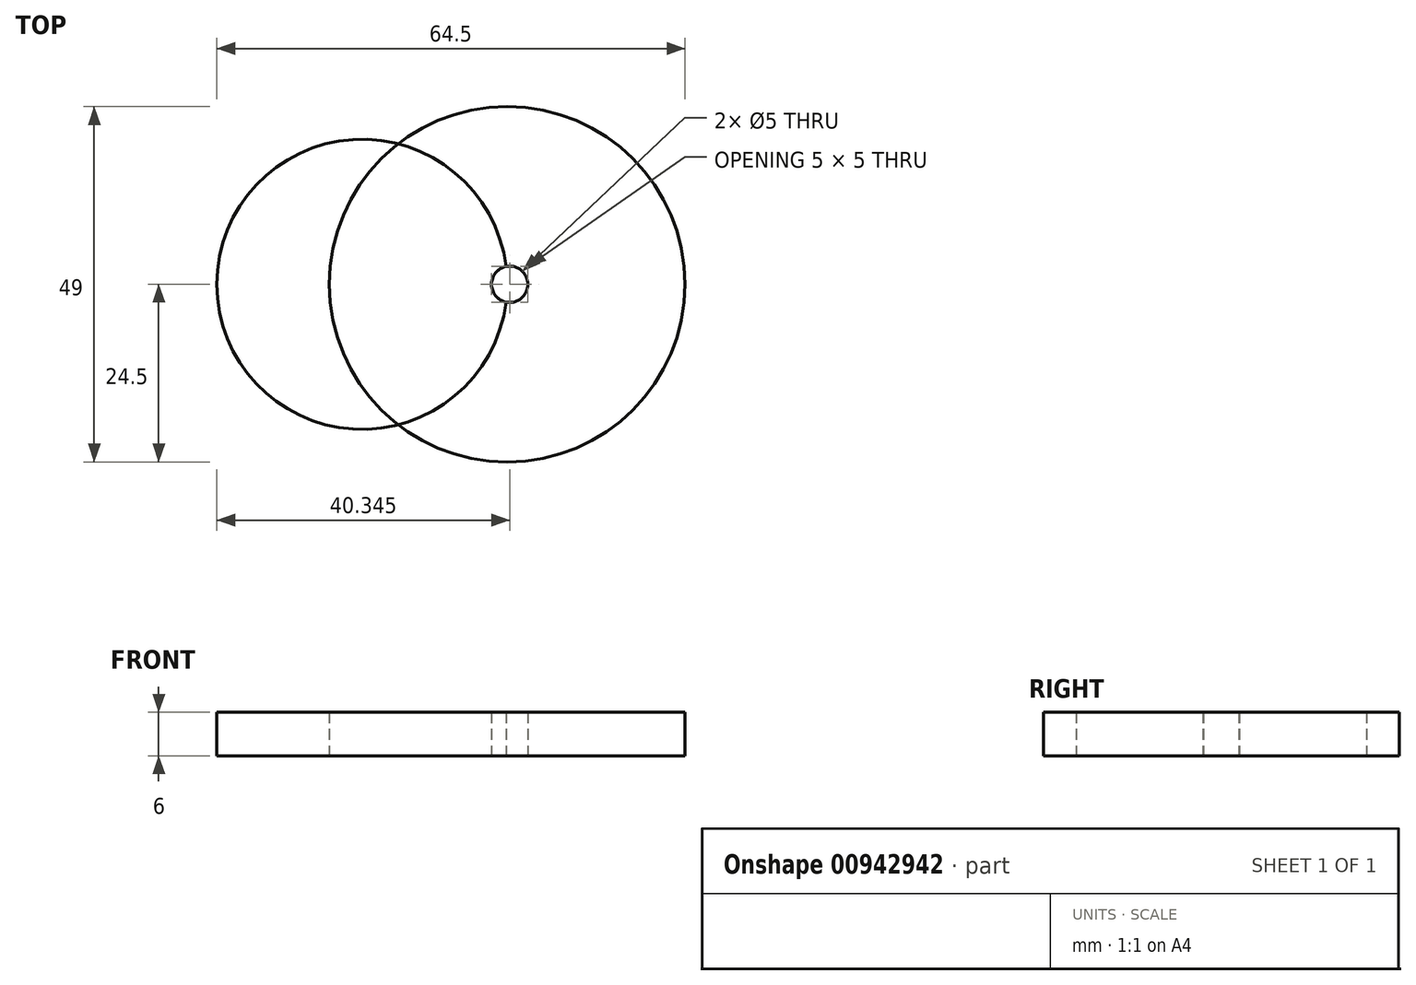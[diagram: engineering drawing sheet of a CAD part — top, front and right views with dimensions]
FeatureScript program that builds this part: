
annotation { "Feature Type Name" : "Feature", "Feature Type Description" : "" }
export const myFeature = defineFeature(function(context is Context, id is Id, definition is map)
    precondition{}
    {
        {
            var Q0;
            Q0=qCreatedBy(makeId("Top.planeOp"),FACE);
            var sketch = newSketch(context, id + "F0", { "sketchPlane" : qUnion([Q0])});
            skCircle(sketch, "E0", {"center": v(0, 0) * mm, "radius": 20 * mm});
            skSolve(sketch);
        }
        {
            var Q0;
            Q0 = qSketchRegion(id + "F0", true);
            extrude(context, id + "F1", {"entities" : qUnion([Q0]), "depth" : 6 * mm, "offsetDistance" : 25 * mm});
        }
        {
            var Q0;
            Q0=qCreatedBy(makeId("Front.planeOp"),FACE);
            var sketch = newSketch(context, id + "F2", { "sketchPlane" : qUnion([Q0])});
            skArc(sketch, "E1", {"start": v(0, 12) * mm, "mid": v(-6, 6) * mm, "end": v(0, 0) * mm});
            skSolve(sketch);
        }
        {
            var Q0;
            Q0=sQuery(id+"F2.wireOp",EDGE,"E1");
            var Q1;
            Q1=makeQuery(id+"F1.opExtrude","CAP_EDGE",EDGE,{"disambiguationData":[OSD([sQuery(id+"F0.wireOp",EDGE,"E0")])],"isStart":false});
            revolve(context, id + "F3", {"bodyType" : ToolBodyType.SURFACE, "surfaceOperationType" : NewSurfaceOperationType.NEW, "surfaceEntities" : qUnion([Q0]), "axis" : qUnion([Q1]), "revolveType" : RevolveType.FULL});
        }
        {
            var Q0;
            Q0=qCreatedBy(makeId("Top.planeOp"),FACE);
            var sketch = newSketch(context, id + "F4", { "sketchPlane" : qUnion([Q0])});
            skCircle(sketch, "E2", {"center": v(20, 0) * mm, "radius": 24.5 * mm});
            skSolve(sketch);
        }
        {
            var Q0;
            Q0 = qSketchRegion(id + "F4", true);
            extrude(context, id + "F5", {"entities" : qUnion([Q0]), "depth" : 6 * mm, "offsetDistance" : 25 * mm});
        }
        {
            var Q0;
            Q0=makeQuery(id+"F3.opRevolve","SWEPT_BODY",BODY,{"disambiguationData":[OSD([sQuery(id+"F2.wireOp",EDGE,"E1")])]});
            var Q1;
            Q1=makeQuery(id+"F5.opExtrude","CAP_EDGE",EDGE,{"disambiguationData":[OSD([sQuery(id+"F4.wireOp",EDGE,"E2")])],"isStart":false});
            circularPattern(context, id + "F6", {"entities" : qUnion([Q0]), "axis" : qUnion([Q1]), "angle" : 360 * degree, "instanceCount" : 6, "equalSpace" : true});
        }
        {
            var Q0;
            Q0=qCreatedBy(makeId("Top.planeOp"),FACE);
            var sketch = newSketch(context, id + "F7", { "sketchPlane" : qUnion([Q0])});
            skPoint(sketch, "E3", {"position": v(20.34, 0) * mm});
            skSolve(sketch);
        }
        {
            var Q0;
            Q0=sQuery(id+"F7.wireOp",VERTEX,"E3");
            var Q1;
            Q1=makeQuery(id+"F1.opExtrude","SWEPT_BODY",BODY,{"disambiguationData":[OSD([sQuery(id+"F0.wireOp",EDGE,"E0")])]});
            var Q2;
            Q2=makeQuery(id+"F5.opExtrude","SWEPT_BODY",BODY,{"disambiguationData":[OSD([sQuery(id+"F4.wireOp",EDGE,"E2")])]});
            hole(context, id + "F8", {"style" : HoleStyle.SIMPLE, "endStyle" : HoleEndStyle.THROUGH, "oppositeDirection" : true, "holeDiameter" : 5 * mm, "majorDiameter" : 5 * mm, "isTappedThrough" : true, "tappedDepth" : 12 * mm, "tapClearance" : 3, "locations" : qUnion([Q0]), "scope" : qUnion([Q1, Q2])});
        }
    });
